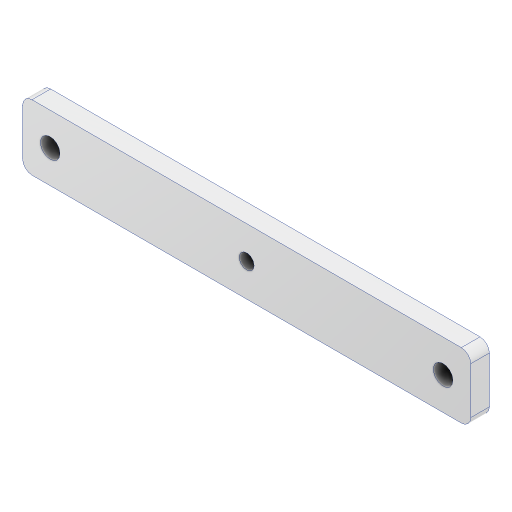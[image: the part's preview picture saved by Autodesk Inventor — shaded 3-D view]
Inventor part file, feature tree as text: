
AUTODESK INVENTOR PART (.ipt)
format: ipt  version: 2023.2 (Build 272271000, 271)  size: 185,856 bytes
history: native  units: mm
features: extrude x7, sketch x7, projected_geometry x5, fillet x2, other x1
ambient origin geometry x8: Origin, YZ Plane, XZ Plane, XY Plane, X Axis, Y Axis, Z Axis, Center Point
bodies: Body1 (feature_tree)
feature tree (22):
  other  "솔리드1"
  extrude  "돌출1"  Depth=96.0mm
  extrude  "돌출2"  Depth=14.0mm
  fillet  "모깎기1"  Radius=4.0mm
  extrude  "돌출3"  Depth=4.2mm
  extrude  "돌출5"  Depth=4.2mm
  extrude  "돌출6"  Depth=84.2mm
  extrude  "돌출7"  Depth=5.9mm
  fillet  "모깎기2"  Radius=4.0mm
  extrude  "돌출8"  Depth=7.0mm
  sketch  "스케치1"
  sketch  "스케치2"
  projected_geometry  "투영된 루프1"
  sketch  "스케치3"
  sketch  "스케치5"
  projected_geometry  "투영된 루프3"
  sketch  "스케치6"
  projected_geometry  "투영된 루프4"
  sketch  "스케치8"
  projected_geometry  "투영된 루프6"
  sketch  "스케치10"
  projected_geometry  "투영된 루프7"
